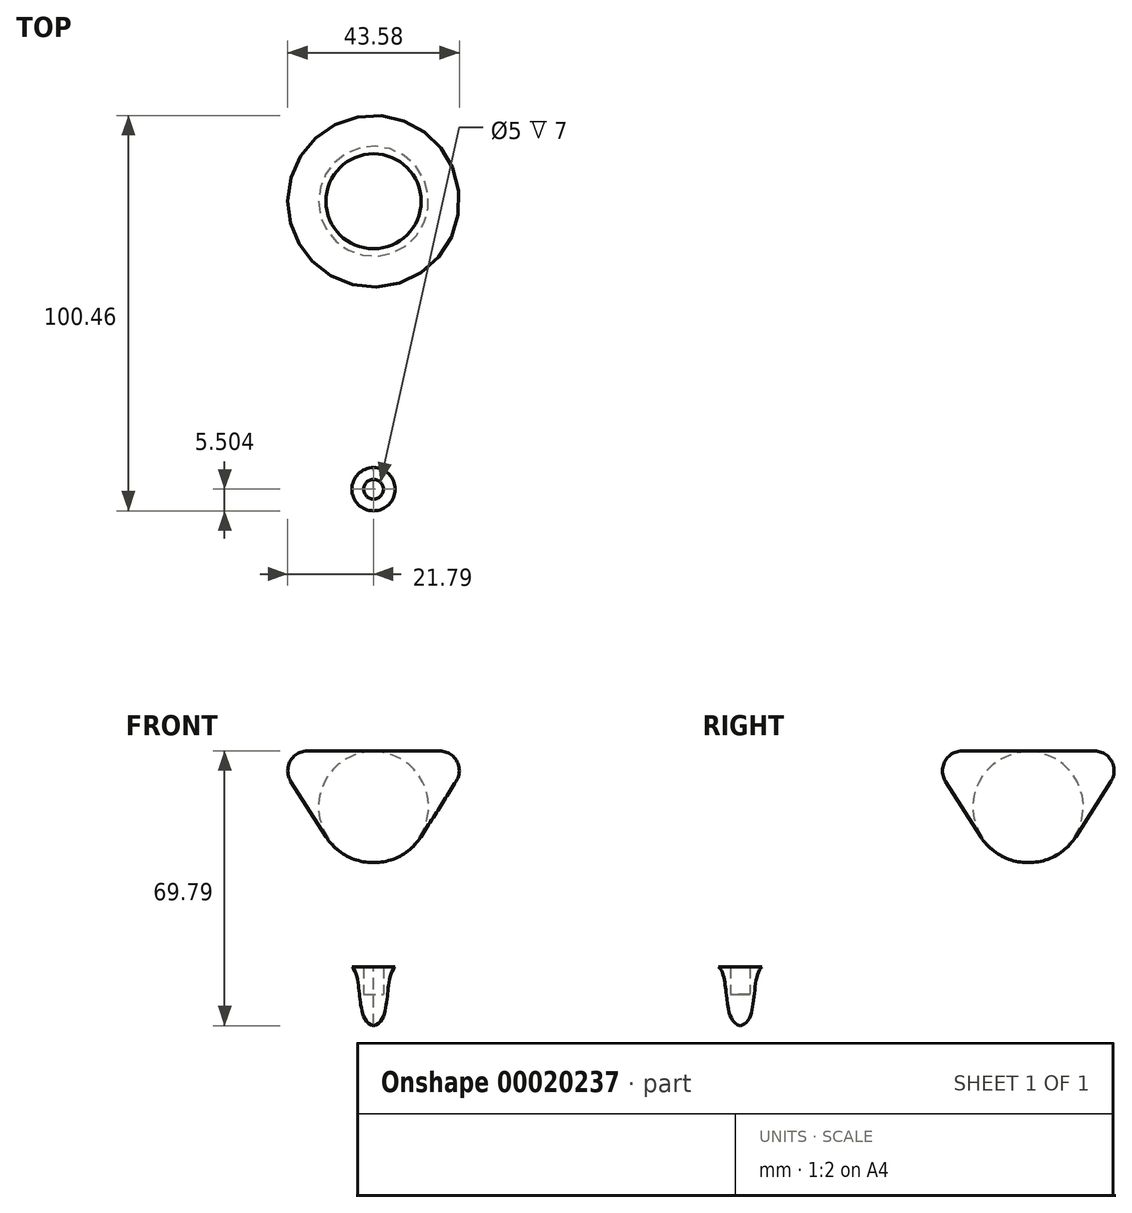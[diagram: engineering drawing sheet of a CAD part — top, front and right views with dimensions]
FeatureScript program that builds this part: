
annotation { "Feature Type Name" : "Feature", "Feature Type Description" : "" }
export const myFeature = defineFeature(function(context is Context, id is Id, definition is map)
    precondition{}
    {
        {
            var Q0;
            Q0=qCreatedBy(makeId("Right.planeOp"),FACE);
            var sketch = newSketch(context, id + "F0", { "sketchPlane" : qUnion([Q0])});
            skLineSegment(sketch, "E0.bottom", {"start": v(32.74, -59.46) * mm, "end": v(52.36, -59.46) * mm, "construction": true});
            skLineSegment(sketch, "E0.top", {"start": v(32.74, -30.46) * mm, "end": v(52.36, -30.46) * mm});
            skLineSegment(sketch, "E0.left", {"start": v(32.74, -43.15) * mm, "end": v(32.74, -30.46) * mm});
            skLineSegment(sketch, "E0.right", {"start": v(52.36, -59.46) * mm, "end": v(52.36, -30.46) * mm, "construction": true});
            skLineSegment(sketch, "E1", {"start": v(41.88, -45.95) * mm, "end": v(52.36, -30.46) * mm});
            skPoint(sketch, "E2.visualSharp", {"position": v(32.74, -59.46) * mm});
            skArc(sketch, "E2.filletArc", {"start": v(32.74, -43.15) * mm, "mid": v(36.27, -47.93) * mm, "end": v(41.88, -45.95) * mm});
            skSolve(sketch);
        }
        {
            var Q0;
            Q0=makeQuery(id+"F0.imprint","IMPRINT",FACE,{"disambiguationData":[TD([[makeQuery(id+"F0.imprint","IMPRINT",EDGE,{"derivedFrom":sQuery(id+"F0.wireOp",EDGE,"E0.top")}),-1.0]])]});
            var Q1;
            Q1=sQuery(id+"F0.wireOp",EDGE,"E0.left");
            revolve(context, id + "F1", {"entities" : qUnion([Q0]), "axis" : qUnion([Q1]), "revolveType" : RevolveType.FULL});
        }
        {
            var Q0;
            Q0=makeQuery(id+"F1.opRevolve","SWEPT_EDGE",EDGE,{"disambiguationData":[OSD([sQuery(id+"F0.wireOp",EDGE,"E0.top"),sQuery(id+"F0.wireOp",EDGE,"E1")])]});
            fillet(context, id + "F2", {"entities" : qUnion([Q0]), "radius" : 5 * mm, "tangentPropagation" : true, "allowEdgeOverflow" : false});
        }
        {
            var Q0;
            Q0=qCreatedBy(makeId("Right.planeOp"),FACE);
            var sketch = newSketch(context, id + "F3", { "sketchPlane" : qUnion([Q0])});
            skArc(sketch, "E3", {"start": v(24.52, 1.7) * mm, "mid": v(31.4, 3.42) * mm, "end": v(36.6, 8.26) * mm});
            skLineSegment(sketch, "E4", {"start": v(24.52, 1.7) * mm, "end": v(24.52, 29.94) * mm});
            skLineSegment(sketch, "E5.bottom", {"start": v(24.52, 29.94) * mm, "end": v(36.6, 29.94) * mm});
            skLineSegment(sketch, "E5.left", {"start": v(24.52, 29.94) * mm, "end": v(24.52, 8.26) * mm});
            skLineSegment(sketch, "E6", {"start": v(36.6, 8.26) * mm, "end": v(50.53, 30.25) * mm});
            skLineSegment(sketch, "E7", {"start": v(50.53, 30.25) * mm, "end": v(36.6, 29.94) * mm});
            skArc(sketch, "E8.trimOffspring", {"start": v(24.82, 29.94) * mm, "mid": v(24.67, 29.94) * mm, "end": v(24.52, 29.94) * mm});
            skSolve(sketch);
        }
        {
            var Q0;
            Q0=makeQuery(id+"F3.imprint","IMPRINT",FACE,{"disambiguationData":[TD([[makeQuery(id+"F3.imprint","IMPRINT",EDGE,{"derivedFrom":sQuery(id+"F3.wireOp",EDGE,"E3")}),1.0]])]});
            var Q1;
            Q1=sQuery(id+"F3.wireOp",EDGE,"E5.left");
            revolve(context, id + "F4", {"entities" : qUnion([Q0]), "axis" : qUnion([Q1]), "revolveType" : RevolveType.FULL});
        }
        {
            var Q0;
            Q0=makeQuery(id+"F4.opRevolve","SWEPT_EDGE",EDGE,{"disambiguationData":[OSD([sQuery(id+"F3.wireOp",EDGE,"E6"),sQuery(id+"F3.wireOp",EDGE,"E7")])]});
            fillet(context, id + "F5", {"entities" : qUnion([Q0]), "radius" : 5 * mm, "tangentPropagation" : true, "allowEdgeOverflow" : false});
        }
        {
            var Q0;
            Q0=makeQuery(id+"F1.opRevolve","SWEPT_BODY",BODY,{"disambiguationData":[OSD([sQuery(id+"F0.wireOp",EDGE,"E0.top"),sQuery(id+"F0.wireOp",EDGE,"E0.left"),sQuery(id+"F0.wireOp",EDGE,"E1"),sQuery(id+"F0.wireOp",EDGE,"E2.filletArc")])]});
            deleteBodies(context, id + "F6", {"entities" : qUnion([Q0])});
        }
        {
            var Q0;
            Q0=qCreatedBy(makeId("Right.planeOp"),FACE);
            var sketch = newSketch(context, id + "F7", { "sketchPlane" : qUnion([Q0])});
            skCircle(sketch, "E9", {"center": v(-41.13, -40.48) * mm, "radius": 13.84 * mm});
            skSolve(sketch);
        }
        {
            var Q0;
            Q0=makeQuery(id+"F7.imprint","IMPRINT",FACE,{"disambiguationData":[TD([[makeQuery(id+"F7.imprint","IMPRINT",EDGE,{"derivedFrom":sQuery(id+"F7.wireOp",EDGE,"E9")}),1.0]])]});
            extrude(context, id + "F8", {"entities" : qUnion([Q0]), "depth" : 25 * mm});
        }
        {
            var Q0;
            Q0=makeQuery(id+"F8.opExtrude","SWEPT_BODY",BODY,{"disambiguationData":[OSD([sQuery(id+"F7.wireOp",EDGE,"E9")])]});
            deleteBodies(context, id + "F9", {"entities" : qUnion([Q0])});
        }
        {
            var Q0;
            Q0=qCreatedBy(makeId("Front.planeOp"),FACE);
            var sketch = newSketch(context, id + "F10", { "sketchPlane" : qUnion([Q0])});
            skLineSegment(sketch, "E10.bottom", {"start": v(-47.4, -65.93) * mm, "end": v(19.16, -65.93) * mm});
            skLineSegment(sketch, "E10.top", {"start": v(-47.4, -17.06) * mm, "end": v(19.16, -17.06) * mm});
            skLineSegment(sketch, "E10.left", {"start": v(-47.4, -65.93) * mm, "end": v(-47.4, -17.06) * mm});
            skLineSegment(sketch, "E10.right", {"start": v(19.16, -65.93) * mm, "end": v(19.16, -17.06) * mm});
            skSolve(sketch);
        }
        {
            var Q0;
            Q0=makeQuery(id+"F10.imprint","IMPRINT",FACE,{"disambiguationData":[TD([[makeQuery(id+"F10.imprint","IMPRINT",EDGE,{"derivedFrom":sQuery(id+"F10.wireOp",EDGE,"E10.bottom")}),1.0]])]});
            extrude(context, id + "F11", {"entities" : qUnion([Q0]), "depth" : 25 * mm});
        }
        {
            var Q0;
            Q0=makeQuery(id+"F11.opExtrude","CAP_FACE",FACE,{"disambiguationData":[OSD([sQuery(id+"F10.wireOp",EDGE,"E10.bottom"),sQuery(id+"F10.wireOp",EDGE,"E10.top"),sQuery(id+"F10.wireOp",EDGE,"E10.left"),sQuery(id+"F10.wireOp",EDGE,"E10.right")])],"isStart":false});
            var sketch = newSketch(context, id + "F12", { "sketchPlane" : qUnion([Q0])});
            skLineSegment(sketch, "E11.bottom", {"start": v(19.16, -48.92) * mm, "end": v(-32.32, -48.92) * mm});
            skLineSegment(sketch, "E11.top", {"start": v(19.16, -38.4) * mm, "end": v(-32.32, -38.4) * mm});
            skLineSegment(sketch, "E11.left", {"start": v(19.16, -48.92) * mm, "end": v(19.16, -38.4) * mm});
            skLineSegment(sketch, "E11.right", {"start": v(-32.32, -48.92) * mm, "end": v(-32.32, -38.4) * mm});
            skSolve(sketch);
        }
        {
            var Q0;
            Q0=makeQuery(id+"F12.imprint","IMPRINT",FACE,{"disambiguationData":[TD([[makeQuery(id+"F12.imprint","IMPRINT",EDGE,{"derivedFrom":sQuery(id+"F12.wireOp",EDGE,"E11.bottom")}),-1.0]])]});
            extrude(context, id + "F13", {"entities" : qUnion([Q0]), "operationType" : NewBodyOperationType.ADD, "depth" : 3 * mm});
        }
        {
            var Q0;
            Q0=makeQuery(id+"F11.opExtrude","SWEPT_BODY",BODY,{"disambiguationData":[OSD([sQuery(id+"F10.wireOp",EDGE,"E10.bottom"),sQuery(id+"F10.wireOp",EDGE,"E10.top"),sQuery(id+"F10.wireOp",EDGE,"E10.left"),sQuery(id+"F10.wireOp",EDGE,"E10.right")])]});
            deleteBodies(context, id + "F14", {"entities" : qUnion([Q0])});
        }
        {
            var Q0;
            Q0=qCreatedBy(makeId("Right.planeOp"),FACE);
            var sketch = newSketch(context, id + "F15", { "sketchPlane" : qUnion([Q0])});
            skLineSegment(sketch, "E12.top", {"start": v(-46.15, -24.74) * mm, "end": v(-43.15, -24.74) * mm});
            skLineSegment(sketch, "E12.left", {"start": v(-48.65, -39.74) * mm, "end": v(-48.65, -31.74) * mm});
            skLineSegment(sketch, "E13.bottom", {"start": v(-48.65, -31.74) * mm, "end": v(-46.15, -31.74) * mm});
            skLineSegment(sketch, "E13.right", {"start": v(-46.15, -31.74) * mm, "end": v(-46.15, -24.74) * mm});
            skFitSpline(sketch, "E14", {"points": [v(-48.65, -39.74) * mm, v(-43.15, -24.74) * mm], "startDerivative": vector(14.6, 2.8) * mm, "endDerivative": vector(9, 7.92) * mm});
            skSolve(sketch);
        }
        {
            var Q0;
            Q0=makeQuery(id+"F15.imprint","IMPRINT",FACE,{"disambiguationData":[TD([[makeQuery(id+"F15.imprint","IMPRINT",EDGE,{"derivedFrom":sQuery(id+"F15.wireOp",EDGE,"E12.top")}),-1.0]])]});
            var Q1;
            Q1=sQuery(id+"F15.wireOp",EDGE,"E12.left");
            revolve(context, id + "F16", {"entities" : qUnion([Q0]), "axis" : qUnion([Q1]), "revolveType" : RevolveType.FULL});
        }
    });
